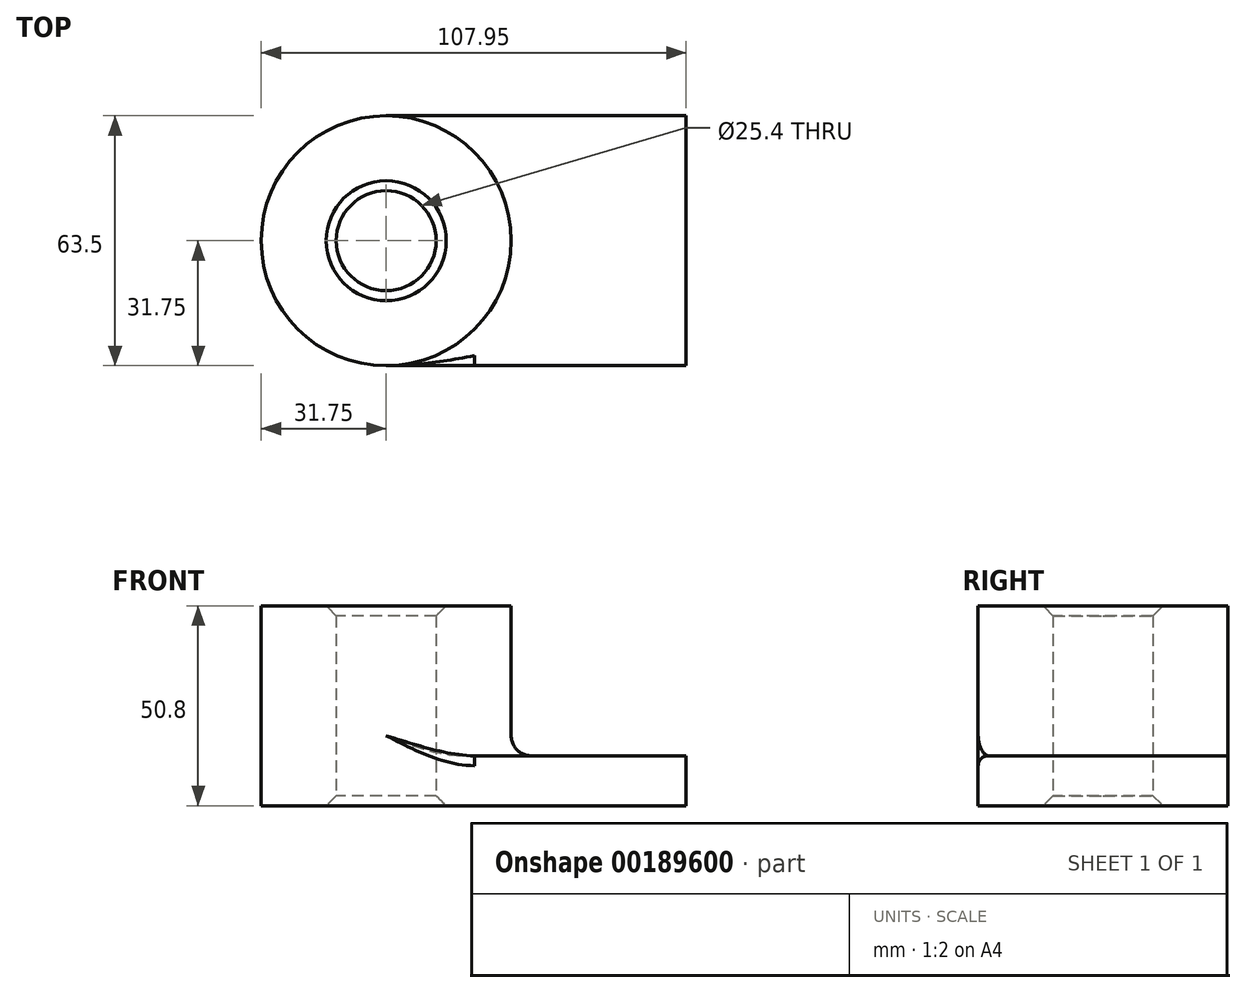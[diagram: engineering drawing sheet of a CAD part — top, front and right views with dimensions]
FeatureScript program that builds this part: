
annotation { "Feature Type Name" : "Feature", "Feature Type Description" : "" }
export const myFeature = defineFeature(function(context is Context, id is Id, definition is map)
    precondition{}
    {
        {
            var Q0;
            Q0=qCreatedBy(makeId("Top.planeOp"),FACE);
            var sketch = newSketch(context, id + "F0", { "sketchPlane" : qUnion([Q0])});
            skLineSegment(sketch, "E0.bottom", {"start": v(38.1, -31.75) * mm, "end": v(-38.1, -31.75) * mm});
            skLineSegment(sketch, "E0.top", {"start": v(38.1, 31.75) * mm, "end": v(-38.1, 31.75) * mm});
            skLineSegment(sketch, "E0.left", {"start": v(38.1, -31.75) * mm, "end": v(38.1, 31.75) * mm});
            skLineSegment(sketch, "E0.right", {"start": v(-38.1, -31.75) * mm, "end": v(-38.1, 31.75) * mm});
            skPoint(sketch, "E0.middle", {"position": v(0, 0) * mm});
            skCircle(sketch, "E1", {"center": v(-38.1, 0) * mm, "radius": 31.75 * mm});
            skCircle(sketch, "E2", {"center": v(-38.1, 0) * mm, "radius": 12.7 * mm});
            skSolve(sketch);
        }
        {
            var Q0;
            Q0 = qSketchRegion(id + "F0", true);
            extrude(context, id + "F1", {"entities" : qUnion([Q0]), "depth" : 12.7 * mm});
        }
        {
            var Q0;
            {var subQ1=sQuery(id+"F0.wireOp",EDGE,"E0.right");var subQ3=sQuery(id+"F0.wireOp",EDGE,"E2");var subQ4=makeQuery(id+"F0.imprint","INTERSECT",VERTEX,{"disambiguationData":[OD(0.0)],"derivedFrom":[subQ1,subQ3]});Q0=makeQuery(id+"F0.imprint","IMPRINT",FACE,{"disambiguationData":[TD([[makeQuery(id+"F0.imprint","IMPRINT",EDGE,{"disambiguationData":[TD([[subQ4,1.0]])],"derivedFrom":subQ3}),-1.0]])]});}
            var Q1;
            {var subQ1=sQuery(id+"F0.wireOp",EDGE,"E0.right");var subQ3=sQuery(id+"F0.wireOp",EDGE,"E2");var subQ4=makeQuery(id+"F0.imprint","INTERSECT",VERTEX,{"disambiguationData":[OD(0.0)],"derivedFrom":[subQ1,subQ3]});Q1=makeQuery(id+"F0.imprint","IMPRINT",FACE,{"disambiguationData":[TD([[makeQuery(id+"F0.imprint","IMPRINT",EDGE,{"disambiguationData":[TD([[subQ4,-1.0]])],"derivedFrom":subQ3}),-1.0]])]});}
            extrude(context, id + "F2", {"entities" : qUnion([Q0, Q1]), "operationType" : NewBodyOperationType.ADD, "depth" : 50.8 * mm});
        }
        {
            var Q0;
            Q0=makeQuery(id+"F3.opExtrude","SWEPT_EDGE",EDGE,{"disambiguationData":[OSD([sQuery(id+"FkjCHYJpF5Iqchb_1.wireOp",EDGE,"HjsJjwTX-Pq9i-Uccz-QjyI-63xcfF5VeI5i.top"),sQuery(id+"FkjCHYJpF5Iqchb_1.wireOp",EDGE,"HjsJjwTX-Pq9i-Uccz-QjyI-63xcfF5VeI5i.left")])]});
            var Q1;
            Q1=makeQuery(id+"F3.opExtrude","SWEPT_EDGE",EDGE,{"disambiguationData":[OSD([sQuery(id+"FkjCHYJpF5Iqchb_1.wireOp",EDGE,"HjsJjwTX-Pq9i-Uccz-QjyI-63xcfF5VeI5i.top"),sQuery(id+"FkjCHYJpF5Iqchb_1.wireOp",EDGE,"HjsJjwTX-Pq9i-Uccz-QjyI-63xcfF5VeI5i.right")])]});
            var Q2;
            Q2=makeQuery(id+"F3.opExtrude","CAP_EDGE",EDGE,{"disambiguationData":[OSD([sQuery(id+"FkjCHYJpF5Iqchb_1.wireOp",EDGE,"HjsJjwTX-Pq9i-Uccz-QjyI-63xcfF5VeI5i.bottom")])],"isStart":false});
            var Q3;
            {var subQ0=sQuery(id+"F0.wireOp",EDGE,"E1");Q3=makeQuery(id+"F2.boolean.opBoolean","INTERSECT",EDGE,{"derivedFrom":[makeQuery(id+"F1.opExtrude","CAP_FACE",FACE,{"disambiguationData":[OSD([sQuery(id+"F0.wireOp",EDGE,"E0.bottom"),sQuery(id+"F0.wireOp",EDGE,"E0.top"),sQuery(id+"F0.wireOp",EDGE,"E0.left"),subQ0,sQuery(id+"F0.wireOp",EDGE,"E2")])],"isStart":false}),makeQuery(id+"F2.opExtrude","SWEPT_FACE",FACE,{"disambiguationData":[OSD([subQ0])]})]});}
            fillet(context, id + "F4", {"entities" : qUnion([Q0, Q1, Q2, Q3]), "radius" : 5.08 * mm, "tangentPropagation" : true, "allowEdgeOverflow" : false});
        }
        {
            var Q0;
            {var subQ0=sQuery(id+"F0.wireOp",EDGE,"E2");Q0=makeQuery(id+"F2.boolean.opBoolean","MERGE",FACE,{"derivedFrom":[makeQuery(id+"F1.opExtrude","SWEPT_FACE",FACE,{"disambiguationData":[OSD([subQ0])]}),makeQuery(id+"F2.opExtrude","SWEPT_FACE",FACE,{"disambiguationData":[OSD([subQ0])]})]});}
            chamfer(context, id + "F5", {"entities" : qUnion([Q0]), "width" : 2.54 * mm, "tangentPropagation" : true});
        }
        {
            var Q0;
            Q0=makeQuery(id+"F3.boolean.opBoolean","MERGE",EDGE,{"derivedFrom":[makeQuery(id+"F1.opExtrude","CAP_EDGE",EDGE,{"disambiguationData":[OSD([sQuery(id+"F0.wireOp",EDGE,"E0.bottom")])],"isStart":false}),makeQuery(id+"F3.opExtrude","SWEPT_EDGE",EDGE,{"disambiguationData":[OSD([sQuery(id+"FkjCHYJpF5Iqchb_1.wireOp",EDGE,"HjsJjwTX-Pq9i-Uccz-QjyI-63xcfF5VeI5i.bottom"),sQuery(id+"FkjCHYJpF5Iqchb_1.wireOp",EDGE,"HjsJjwTX-Pq9i-Uccz-QjyI-63xcfF5VeI5i.left")])]})]});
            fillet(context, id + "F6", {"entities" : qUnion([Q0]), "radius" : 2.54 * mm, "tangentPropagation" : true, "allowEdgeOverflow" : false});
        }
    });
